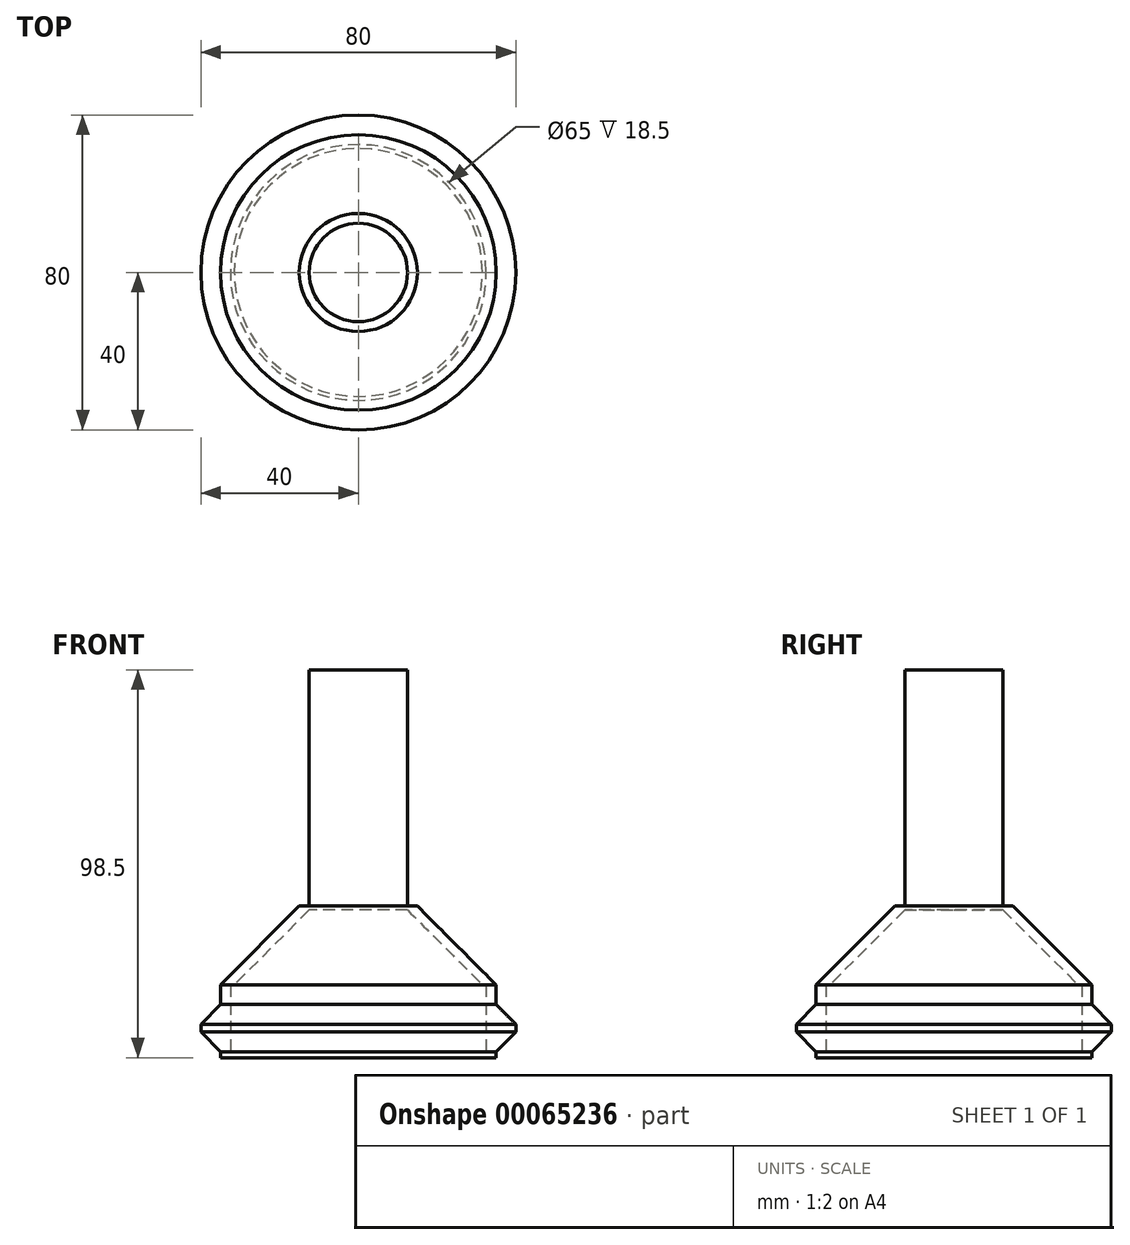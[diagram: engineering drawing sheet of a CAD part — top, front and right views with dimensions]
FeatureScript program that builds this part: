
annotation { "Feature Type Name" : "Feature", "Feature Type Description" : "" }
export const myFeature = defineFeature(function(context is Context, id is Id, definition is map)
    precondition{}
    {
        {
            var Q0;
            Q0=qCreatedBy(makeId("Top.planeOp"),FACE);
            var sketch = newSketch(context, id + "F0", { "sketchPlane" : qUnion([Q0])});
            skCircle(sketch, "E0", {"center": v(0, 0) * mm, "radius": 32.5 * mm});
            skCircle(sketch, "E1.0", {"center": v(0, 0) * mm, "radius": 35 * mm});
            skCircle(sketch, "E2", {"center": v(0, 0) * mm, "radius": 12.5 * mm});
            skCircle(sketch, "E3.0", {"center": v(0, 0) * mm, "radius": 40 * mm});
            skSolve(sketch);
        }
        {
            var Q0;
            Q0=makeQuery(id+"F0.imprint","IMPRINT",FACE,{"disambiguationData":[TD([[makeQuery(id+"F0.imprint","IMPRINT",EDGE,{"derivedFrom":sQuery(id+"F0.wireOp",EDGE,"E0")}),-1.0]])]});
            extrude(context, id + "F1", {"entities" : qUnion([Q0]), "depth" : 40 * mm});
        }
        {
            var Q0;
            Q0=makeQuery(id+"F0.imprint","IMPRINT",FACE,{"disambiguationData":[TD([[makeQuery(id+"F0.imprint","IMPRINT",EDGE,{"derivedFrom":sQuery(id+"F0.wireOp",EDGE,"E0")}),1.0]])]});
            extrude(context, id + "F2", {"entities" : qUnion([Q0]), "operationType" : NewBodyOperationType.ADD, "depth" : 40 * mm, "hasSecondDirection" : true, "secondDirectionOppositeDirection" : false, "secondDirectionDepth" : 20 * mm});
        }
        {
            var Q0;
            Q0=makeQuery(id+"F0.imprint","IMPRINT",FACE,{"disambiguationData":[TD([[makeQuery(id+"F0.imprint","IMPRINT",EDGE,{"derivedFrom":sQuery(id+"F0.wireOp",EDGE,"E2")}),1.0]])]});
            extrude(context, id + "F3", {"entities" : qUnion([Q0]), "operationType" : NewBodyOperationType.ADD, "depth" : 100 * mm, "hasSecondDirection" : true, "secondDirectionOppositeDirection" : false, "secondDirectionDepth" : 39 * mm});
        }
        {
            var Q0;
            Q0=makeQuery(id+"F1.opExtrude","CAP_EDGE",EDGE,{"disambiguationData":[OSD([sQuery(id+"F0.wireOp",EDGE,"E1.0")])],"isStart":false});
            chamfer(context, id + "F4", {"entities" : qUnion([Q0]), "width" : 20 * mm, "tangentPropagation" : true});
        }
        {
            var Q0;
            Q0=makeQuery(id+"F2.opExtrude","CAP_EDGE",EDGE,{"disambiguationData":[OSD([sQuery(id+"F0.wireOp",EDGE,"E2")])],"isStart":true});
            chamfer(context, id + "F5", {"entities" : qUnion([Q0]), "width" : 19 * mm, "tangentPropagation" : true});
        }
        {
            var Q0;
            Q0=makeQuery(id+"F0.imprint","IMPRINT",FACE,{"disambiguationData":[TD([[makeQuery(id+"F0.imprint","IMPRINT",EDGE,{"derivedFrom":sQuery(id+"F0.wireOp",EDGE,"E1.0")}),-1.0]])]});
            extrude(context, id + "F6", {"entities" : qUnion([Q0]), "operationType" : NewBodyOperationType.ADD, "depth" : 15 * mm, "hasSecondDirection" : true, "secondDirectionOppositeDirection" : false, "secondDirectionDepth" : 3 * mm});
        }
        {
            var Q0;
            Q0=makeQuery(id+"F6.opExtrude","CAP_EDGE",EDGE,{"disambiguationData":[OSD([sQuery(id+"F0.wireOp",EDGE,"E3.0")])],"isStart":true});
            var Q1;
            Q1=makeQuery(id+"F6.opExtrude","CAP_EDGE",EDGE,{"disambiguationData":[OSD([sQuery(id+"F0.wireOp",EDGE,"E3.0")])],"isStart":false});
            chamfer(context, id + "F7", {"entities" : qUnion([Q0, Q1]), "width" : 5 * mm, "tangentPropagation" : true});
        }
        {
            var Q0;
            Q0=makeQuery(id+"F1.opExtrude","CAP_FACE",FACE,{"disambiguationData":[OSD([sQuery(id+"F0.wireOp",EDGE,"E0"),sQuery(id+"F0.wireOp",EDGE,"E1.0")])],"isStart":true});
            extrude(context, id + "F8", {"entities" : qUnion([Q0]), "operationType" : NewBodyOperationType.REMOVE, "oppositeDirection" : true, "depth" : 1.5 * mm, "offsetDistance" : 25 * mm});
        }
    });
